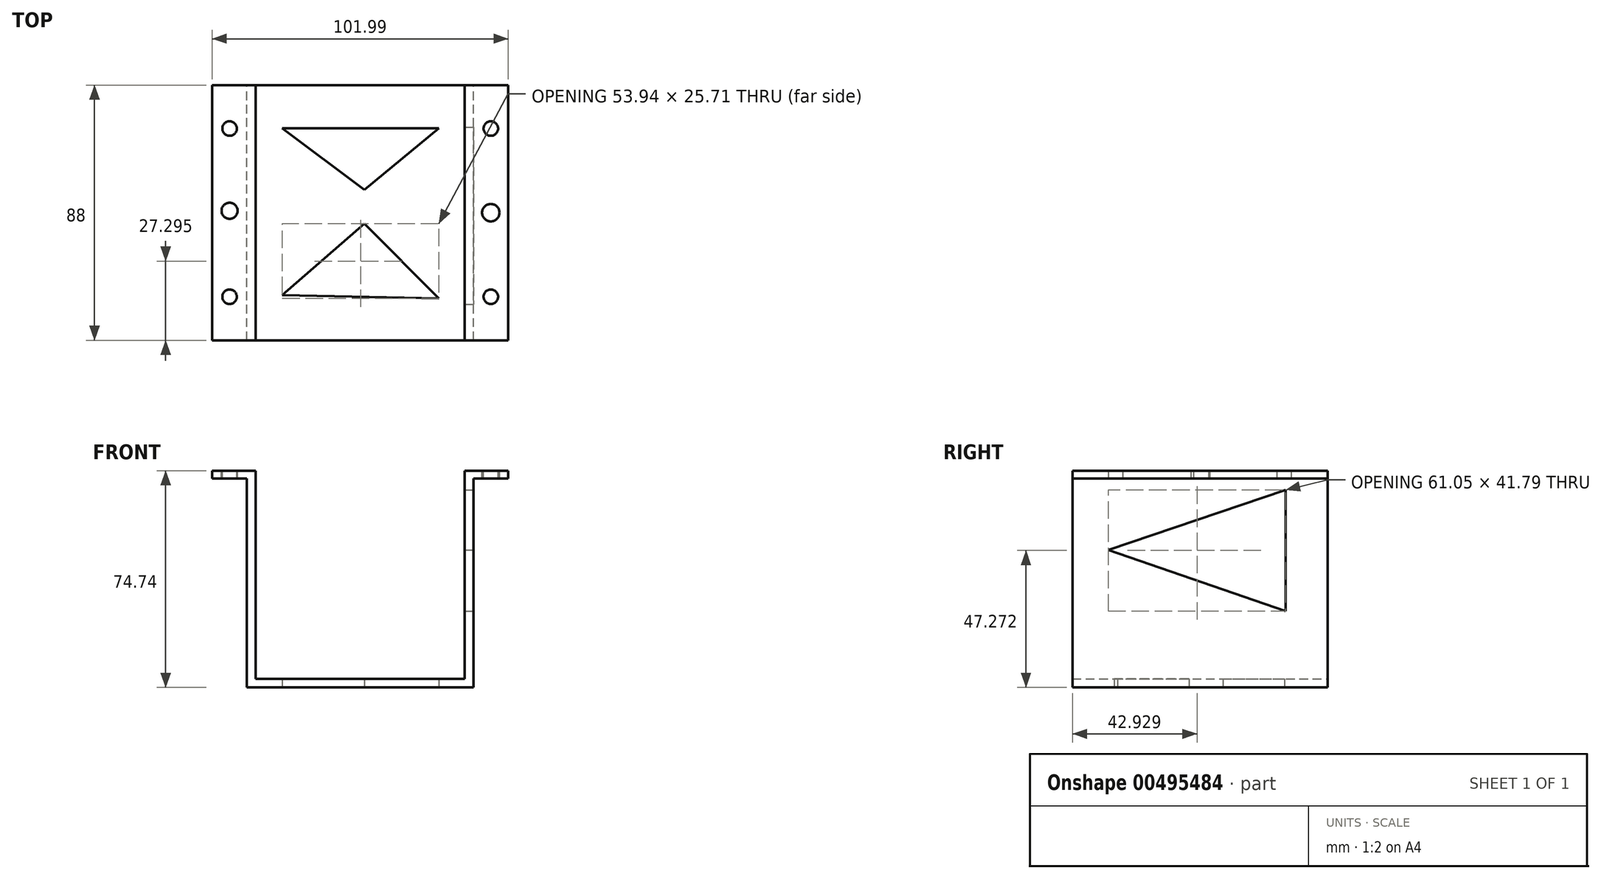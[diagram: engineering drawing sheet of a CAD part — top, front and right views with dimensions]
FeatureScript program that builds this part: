
annotation { "Feature Type Name" : "Feature", "Feature Type Description" : "" }
export const myFeature = defineFeature(function(context is Context, id is Id, definition is map)
    precondition{}
    {
        {
            var Q0;
            Q0=qCreatedBy(makeId("Front.planeOp"),FACE);
            var sketch = newSketch(context, id + "F0", { "sketchPlane" : qUnion([Q0])});
            skLineSegment(sketch, "E0", {"start": v(-2.97, -6.62) * mm, "end": v(-2.97, -9.62) * mm});
            skLineSegment(sketch, "E1", {"start": v(-2.97, -9.62) * mm, "end": v(36.03, -9.62) * mm});
            skLineSegment(sketch, "E2", {"start": v(36.03, -9.62) * mm, "end": v(36.03, 62.38) * mm});
            skLineSegment(sketch, "E3", {"start": v(36.03, 62.38) * mm, "end": v(48.02, 62.38) * mm});
            skLineSegment(sketch, "E4", {"start": v(48.02, 62.38) * mm, "end": v(48.02, 65.12) * mm});
            skLineSegment(sketch, "E5", {"start": v(48.02, 65.12) * mm, "end": v(33.02, 65.12) * mm});
            skLineSegment(sketch, "E6", {"start": v(33.02, 65.12) * mm, "end": v(33.02, -6.62) * mm});
            skLineSegment(sketch, "E7", {"start": v(33.02, -6.62) * mm, "end": v(-2.97, -6.62) * mm});
            skLineSegment(sketch, "E8.MirrorCS", {"start": v(-53.97, 62.38) * mm, "end": v(-53.97, 65.12) * mm});
            skLineSegment(sketch, "E9.MirrorCS", {"start": v(-41.97, -9.62) * mm, "end": v(-41.97, 62.38) * mm});
            skLineSegment(sketch, "E10.MirrorCS", {"start": v(-41.97, 62.38) * mm, "end": v(-53.97, 62.38) * mm});
            skLineSegment(sketch, "E11.MirrorCS", {"start": v(-53.97, 65.12) * mm, "end": v(-38.97, 65.12) * mm});
            skLineSegment(sketch, "E12.MirrorCS", {"start": v(-38.97, 65.12) * mm, "end": v(-38.97, -6.62) * mm});
            skLineSegment(sketch, "E13.MirrorCS", {"start": v(-2.97, -9.62) * mm, "end": v(-41.97, -9.62) * mm});
            skLineSegment(sketch, "E14.MirrorCS", {"start": v(-38.97, -6.62) * mm, "end": v(-2.97, -6.62) * mm});
            skPoint(sketch, "E15.MirrorCS.start.orphan", {"position": v(36.03, 62.38) * mm});
            skSolve(sketch);
        }
        {
            var Q0;
            Q0=qSketchRegion(id+"F0",true);
            extrude(context, id + "F1", {"entities" : qUnion([Q0]), "endBound" : BoundingType.SYMMETRIC, "depth" : 88 * mm});
        }
        {
            var Q0;
            Q0=makeQuery(id+"F1.opExtrude","SWEPT_FACE",FACE,{"disambiguationData":[OSD([sQuery(id+"F0.wireOp",EDGE,"E5")])]});
            var sketch = newSketch(context, id + "F2", { "sketchPlane" : qUnion([Q0])});
            skLineSegment(sketch, "E16", {"start": v(42.02, -44) * mm, "end": v(42.02, 34) * mm, "construction": true});
            skLineSegment(sketch, "E17.0.0", {"start": v(-38.97, 44) * mm, "end": v(-53.97, 44) * mm, "construction": true});
            skLineSegment(sketch, "E17.0.1", {"start": v(-53.97, 44) * mm, "end": v(-53.97, -44) * mm, "construction": true});
            skLineSegment(sketch, "E17.0.2", {"start": v(-53.97, -44) * mm, "end": v(-38.97, -44) * mm, "construction": true});
            skLineSegment(sketch, "E17.0.3", {"start": v(-38.97, -44) * mm, "end": v(-38.97, 44) * mm, "construction": true});
            skLineSegment(sketch, "E18", {"start": v(-47.97, 34) * mm, "end": v(-47.97, -44) * mm, "construction": true});
            skLineSegment(sketch, "E19", {"start": v(-53.97, -29) * mm, "end": v(48.02, -29) * mm, "construction": true});
            skLineSegment(sketch, "E20", {"start": v(48.02, 29) * mm, "end": v(-53.97, 29) * mm, "construction": true});
            skLineSegment(sketch, "E21", {"start": v(48.02, -29) * mm, "end": v(48.02, -44) * mm, "construction": true});
            skLineSegment(sketch, "E22", {"start": v(48.02, 44) * mm, "end": v(48.02, 29) * mm, "construction": true});
            skCircle(sketch, "E23", {"center": v(42.02, -29) * mm, "radius": 2.5 * mm});
            skCircle(sketch, "E24", {"center": v(42.02, 29) * mm, "radius": 2.5 * mm});
            skCircle(sketch, "E25", {"center": v(-47.97, 29) * mm, "radius": 2.5 * mm});
            skCircle(sketch, "E26", {"center": v(-47.97, -29) * mm, "radius": 2.5 * mm});
            skCircle(sketch, "E27", {"center": v(-47.97, 0.65) * mm, "radius": 2.78 * mm});
            skCircle(sketch, "E28", {"center": v(42.02, 0) * mm, "radius": 3 * mm});
            skPoint(sketch, "E28.centerSnap0", {"position": v(48.02, 0) * mm});
            skSolve(sketch);
        }
        {
            var Q0;
            Q0=qSketchRegion(id+"F2",true);
            extrude(context, id + "F3", {"entities" : qUnion([Q0]), "operationType" : NewBodyOperationType.REMOVE, "endBound" : BoundingType.UP_TO_NEXT, "oppositeDirection" : true, "depth" : 25 * mm});
        }
        {
            var Q0;
            Q0=makeQuery(id+"F1.opExtrude","SWEPT_FACE",FACE,{"disambiguationData":[OSD([sQuery(id+"F0.wireOp",EDGE,"E1"),sQuery(id+"F0.wireOp",EDGE,"E13.MirrorCS")])]});
            var sketch = newSketch(context, id + "F4", { "sketchPlane" : qUnion([Q0])});
            skLineSegment(sketch, "E29", {"start": v(24.14, 29.56) * mm, "end": v(-1.58, 3.85) * mm});
            skLineSegment(sketch, "E30", {"start": v(-1.58, 3.85) * mm, "end": v(-29.8, 28.44) * mm});
            skLineSegment(sketch, "E31", {"start": v(-29.8, 28.44) * mm, "end": v(24.14, 29.56) * mm});
            skLineSegment(sketch, "E32", {"start": v(-1.58, -7.9) * mm, "end": v(24.14, -29.13) * mm});
            skLineSegment(sketch, "E33", {"start": v(24.14, -29.13) * mm, "end": v(-29.8, -29.13) * mm});
            skLineSegment(sketch, "E34", {"start": v(-29.8, -29.13) * mm, "end": v(-1.58, -7.9) * mm});
            skSolve(sketch);
        }
        {
            var Q0;
            Q0 = qSketchRegion(id + "F4", true);
            extrude(context, id + "F5", {"entities" : qUnion([Q0]), "operationType" : NewBodyOperationType.REMOVE, "oppositeDirection" : true, "depth" : 4 * mm});
        }
        {
            var Q0;
            Q0=makeQuery(id+"F1.opExtrude","SWEPT_FACE",FACE,{"disambiguationData":[OSD([sQuery(id+"F0.wireOp",EDGE,"E2")])]});
            var sketch = newSketch(context, id + "F6", { "sketchPlane" : qUnion([Q0])});
            skLineSegment(sketch, "E35", {"start": v(44, 58.55) * mm, "end": v(-44, 58.55) * mm, "construction": true});
            skLineSegment(sketch, "E36", {"start": v(-44, 58.55) * mm, "end": v(-44, -5.93) * mm, "construction": true});
            skLineSegment(sketch, "E37", {"start": v(-44, -5.93) * mm, "end": v(44, -5.93) * mm, "construction": true});
            skLineSegment(sketch, "E38", {"start": v(44, -5.93) * mm, "end": v(44, 0.68) * mm, "construction": true});
            skLineSegment(sketch, "E39", {"start": v(44, 0.68) * mm, "end": v(-48.31, 0.68) * mm, "construction": true});
            skLineSegment(sketch, "E40", {"start": v(-48.31, 0.68) * mm, "end": v(-44, 58.55) * mm, "construction": true});
            skLineSegment(sketch, "E41", {"start": v(-44, 49.92) * mm, "end": v(44, 49.92) * mm, "construction": true});
            skLineSegment(sketch, "E42", {"start": v(44, 49.92) * mm, "end": v(44, 58.55) * mm, "construction": true});
            skLineSegment(sketch, "E43", {"start": v(44, 49.92) * mm, "end": v(-44, 0.68) * mm, "construction": true});
            skLineSegment(sketch, "E44", {"start": v(-44, 0.68) * mm, "end": v(-44, 49.92) * mm, "construction": true});
            skLineSegment(sketch, "E45", {"start": v(29.45, 58.55) * mm, "end": v(29.45, 16.76) * mm});
            skLineSegment(sketch, "E46", {"start": v(29.45, 16.76) * mm, "end": v(-31.6, 37.8) * mm});
            skLineSegment(sketch, "E47", {"start": v(-31.6, 37.8) * mm, "end": v(29.45, 58.55) * mm});
            skSolve(sketch);
        }
        {
            var Q0;
            Q0 = qSketchRegion(id + "F6", true);
            extrude(context, id + "F7", {"entities" : qUnion([Q0]), "operationType" : NewBodyOperationType.REMOVE, "oppositeDirection" : true, "depth" : 4 * mm});
        }
    });
